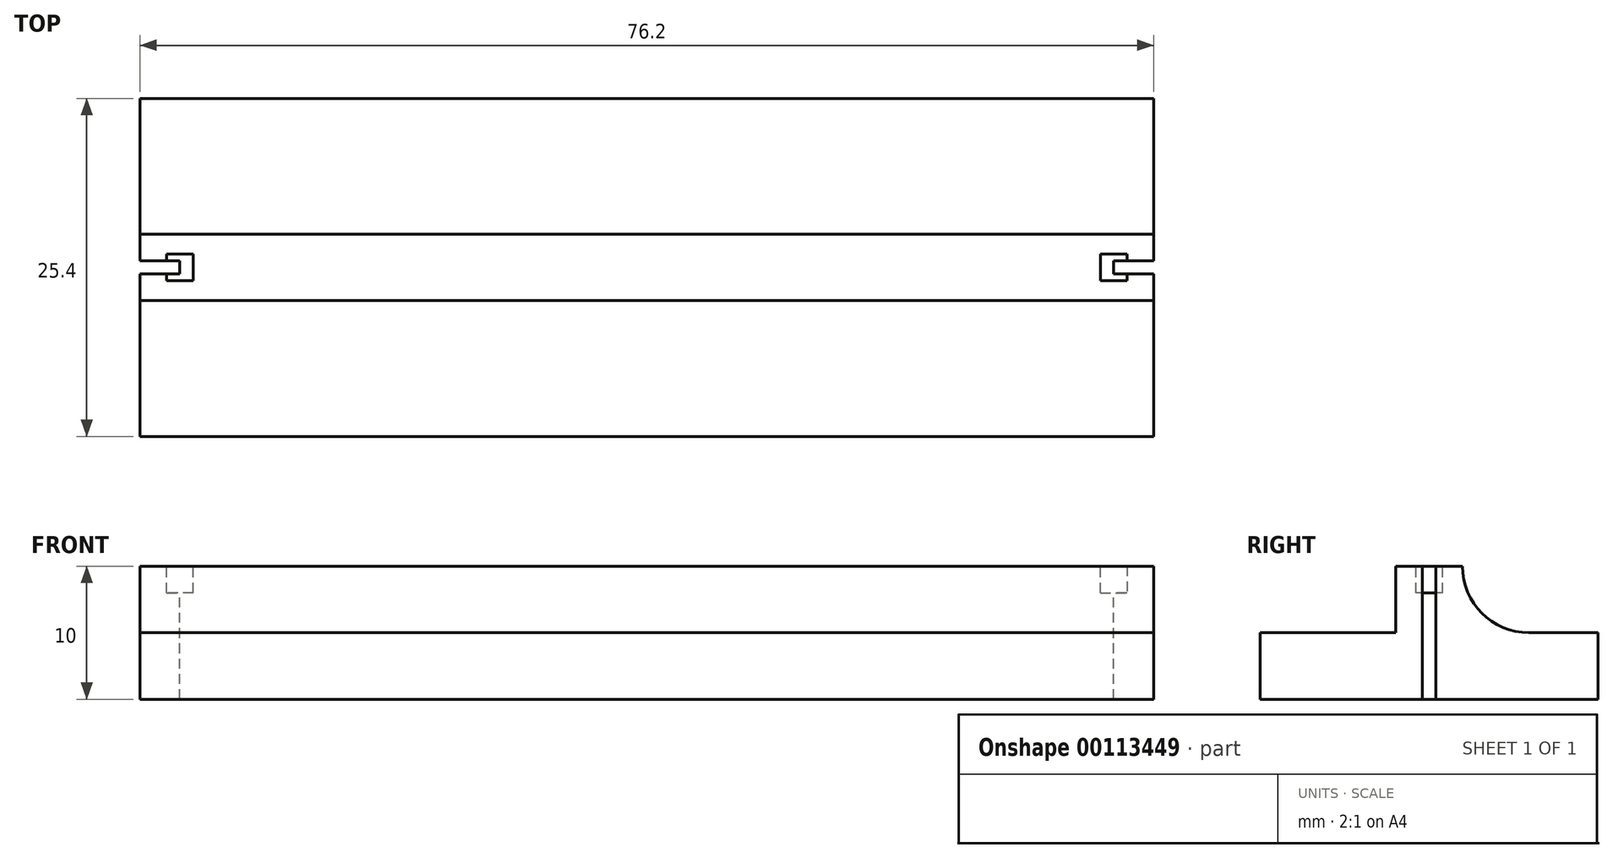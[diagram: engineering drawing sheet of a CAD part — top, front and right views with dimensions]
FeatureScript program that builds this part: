
annotation { "Feature Type Name" : "Feature", "Feature Type Description" : "" }
export const myFeature = defineFeature(function(context is Context, id is Id, definition is map)
    precondition{}
    {
        {
            var Q0;
            Q0=qCreatedBy(makeId("Top.planeOp"),FACE);
            var sketch = newSketch(context, id + "F0", { "sketchPlane" : qUnion([Q0])});
            skLineSegment(sketch, "E0.bottom", {"start": v(-38.1, 12.7) * mm, "end": v(38.1, 12.7) * mm});
            skLineSegment(sketch, "E0.top", {"start": v(-38.1, -12.7) * mm, "end": v(38.1, -12.7) * mm});
            skLineSegment(sketch, "E0.left", {"start": v(-38.1, 12.7) * mm, "end": v(-38.1, -12.7) * mm});
            skLineSegment(sketch, "E0.right", {"start": v(38.1, 12.7) * mm, "end": v(38.1, -12.7) * mm});
            skPoint(sketch, "E0.middle", {"position": v(0, 0) * mm});
            skSolve(sketch);
        }
        {
            var Q0;
            Q0 = qSketchRegion(id + "F0", true);
            extrude(context, id + "F1", {"entities" : qUnion([Q0]), "depth" : 5 * mm});
        }
        {
            var Q0;
            Q0=makeQuery(id+"F1.opExtrude","CAP_FACE",FACE,{"disambiguationData":[OSD([sQuery(id+"F0.wireOp",EDGE,"E0.bottom"),sQuery(id+"F0.wireOp",EDGE,"E0.top"),sQuery(id+"F0.wireOp",EDGE,"E0.left"),sQuery(id+"F0.wireOp",EDGE,"E0.right")])],"isStart":false});
            var sketch = newSketch(context, id + "F2", { "sketchPlane" : qUnion([Q0])});
            skLineSegment(sketch, "E1.bottom", {"start": v(-38.1, 2.5) * mm, "end": v(38.1, 2.5) * mm});
            skLineSegment(sketch, "E1.top", {"start": v(-38.1, -2.5) * mm, "end": v(38.1, -2.5) * mm});
            skLineSegment(sketch, "E1.left", {"start": v(-38.1, 2.5) * mm, "end": v(-38.1, -2.5) * mm});
            skLineSegment(sketch, "E1.right", {"start": v(38.1, 2.5) * mm, "end": v(38.1, -2.5) * mm});
            skPoint(sketch, "E1.middle", {"position": v(0, 0) * mm});
            skSolve(sketch);
        }
        {
            var Q0;
            Q0 = qSketchRegion(id + "F2", true);
            extrude(context, id + "F3", {"entities" : qUnion([Q0]), "operationType" : NewBodyOperationType.ADD, "depth" : 5 * mm});
        }
        {
            var Q0;
            Q0=makeQuery(id+"F3.opExtrude","CAP_EDGE",EDGE,{"disambiguationData":[OSD([sQuery(id+"F2.wireOp",EDGE,"E1.top")])],"isStart":true});
            var Q1;
            Q1=makeQuery(id+"F3.opExtrude","CAP_EDGE",EDGE,{"disambiguationData":[OSD([sQuery(id+"F2.wireOp",EDGE,"E1.bottom")])],"isStart":true});
            fillet(context, id + "F4", {"entities" : qUnion([Q0, Q1]), "radius" : 5 * mm, "tangentPropagation" : true, "allowEdgeOverflow" : false});
        }
        {
            var Q0;
            Q0=makeQuery(id+"F3.opExtrude","CAP_FACE",FACE,{"disambiguationData":[OSD([sQuery(id+"F2.wireOp",EDGE,"E1.bottom"),sQuery(id+"F2.wireOp",EDGE,"E1.top"),sQuery(id+"F2.wireOp",EDGE,"E1.left"),sQuery(id+"F2.wireOp",EDGE,"E1.right")])],"isStart":false});
            var sketch = newSketch(context, id + "F5", { "sketchPlane" : qUnion([Q0])});
            skLineSegment(sketch, "E2.bottom", {"start": v(34.1, 1) * mm, "end": v(36.1, 1) * mm});
            skLineSegment(sketch, "E2.top", {"start": v(34.1, -1) * mm, "end": v(36.1, -1) * mm});
            skLineSegment(sketch, "E2.left", {"start": v(34.1, 1) * mm, "end": v(34.1, -1) * mm});
            skLineSegment(sketch, "E2.right", {"start": v(36.1, 1) * mm, "end": v(36.1, -1) * mm});
            skLineSegment(sketch, "E3.MirrorCS", {"start": v(-34.1, 1) * mm, "end": v(-34.1, -1) * mm});
            skLineSegment(sketch, "E4.MirrorCS", {"start": v(-34.1, 1) * mm, "end": v(-36.1, 1) * mm});
            skLineSegment(sketch, "E5.MirrorCS", {"start": v(-34.1, -1) * mm, "end": v(-36.1, -1) * mm});
            skLineSegment(sketch, "E6.MirrorCS", {"start": v(-36.1, 1) * mm, "end": v(-36.1, -1) * mm});
            skSolve(sketch);
        }
        {
            var Q0;
            Q0=makeQuery(id+"F3.opExtrude","CAP_FACE",FACE,{"disambiguationData":[OSD([sQuery(id+"F2.wireOp",EDGE,"E1.bottom"),sQuery(id+"F2.wireOp",EDGE,"E1.top"),sQuery(id+"F2.wireOp",EDGE,"E1.left"),sQuery(id+"F2.wireOp",EDGE,"E1.right")])],"isStart":false});
            var sketch = newSketch(context, id + "F6", { "sketchPlane" : qUnion([Q0])});
            skLineSegment(sketch, "E7.bottom", {"start": v(38.1, -0.5) * mm, "end": v(35.1, -0.5) * mm});
            skLineSegment(sketch, "E7.top", {"start": v(38.1, 0.5) * mm, "end": v(35.1, 0.5) * mm});
            skLineSegment(sketch, "E7.left", {"start": v(38.1, -0.5) * mm, "end": v(38.1, 0.5) * mm});
            skLineSegment(sketch, "E7.right", {"start": v(35.1, -0.5) * mm, "end": v(35.1, 0.5) * mm});
            skLineSegment(sketch, "E8.MirrorCS", {"start": v(-38.1, -0.5) * mm, "end": v(-35.1, -0.5) * mm});
            skLineSegment(sketch, "E9.MirrorCS", {"start": v(-35.1, -0.5) * mm, "end": v(-35.1, 0.5) * mm});
            skLineSegment(sketch, "E10.MirrorCS", {"start": v(-38.1, 0.5) * mm, "end": v(-35.1, 0.5) * mm});
            skLineSegment(sketch, "E11.MirrorCS", {"start": v(-38.1, -0.5) * mm, "end": v(-38.1, 0.5) * mm});
            skSolve(sketch);
        }
        {
            var Q0;
            Q0 = qSketchRegion(id + "F5", true);
            extrude(context, id + "F7", {"entities" : qUnion([Q0]), "operationType" : NewBodyOperationType.REMOVE, "oppositeDirection" : true, "depth" : 2 * mm});
        }
        {
            var Q0;
            Q0 = qSketchRegion(id + "F6", true);
            extrude(context, id + "F8", {"entities" : qUnion([Q0]), "operationType" : NewBodyOperationType.REMOVE, "endBound" : BoundingType.THROUGH_ALL, "oppositeDirection" : true, "depth" : 25 * mm});
        }
    });
